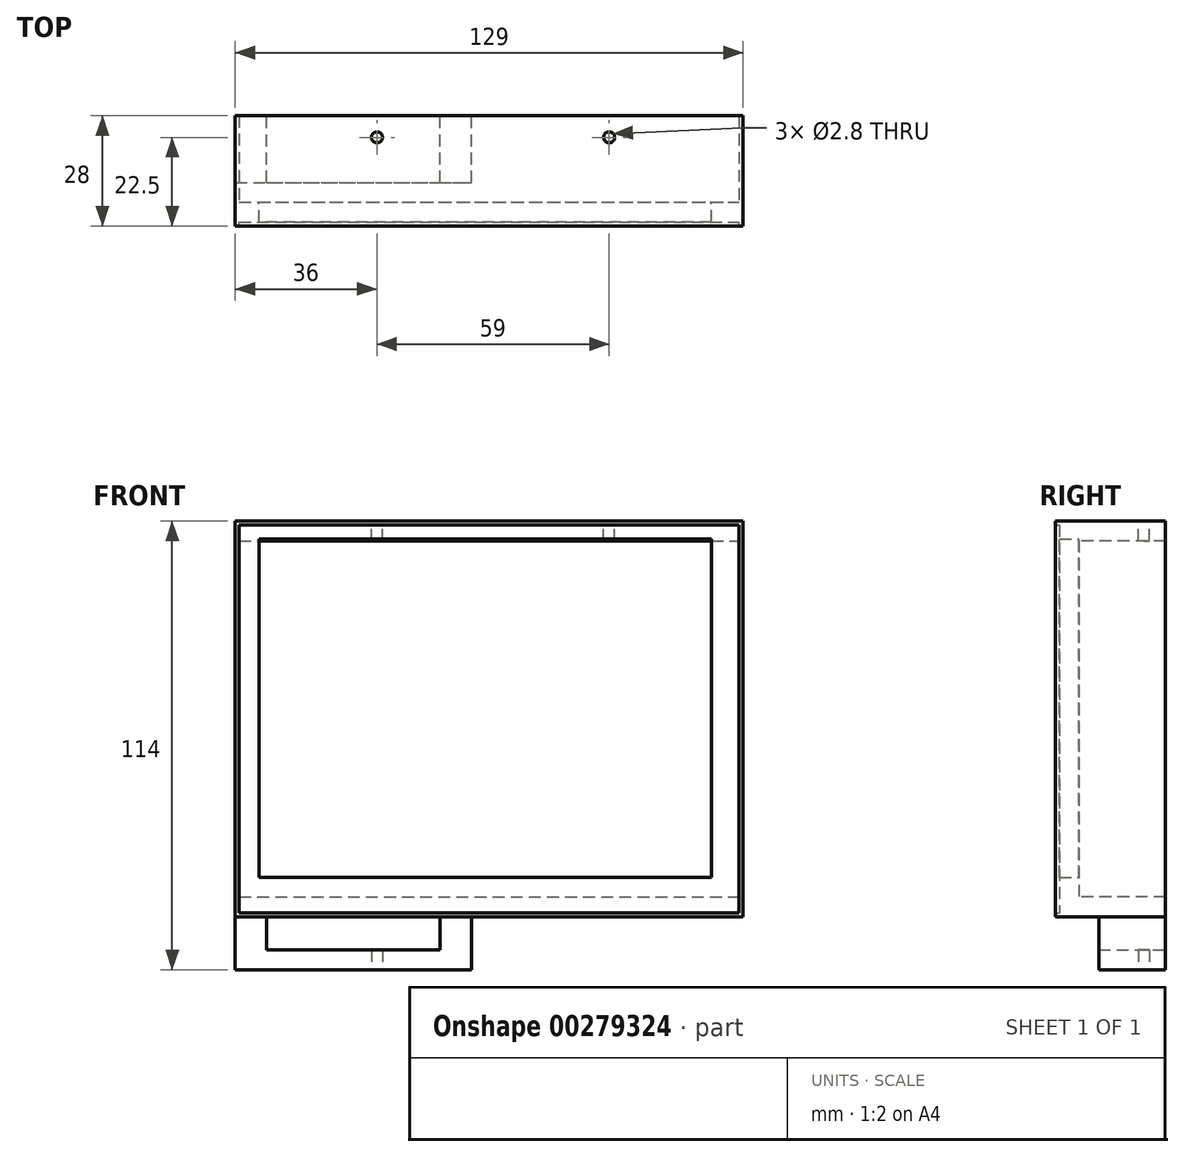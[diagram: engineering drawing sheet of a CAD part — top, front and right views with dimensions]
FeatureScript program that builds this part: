
annotation { "Feature Type Name" : "Feature", "Feature Type Description" : "" }
export const myFeature = defineFeature(function(context is Context, id is Id, definition is map)
    precondition{}
    {
        {
            var Q0;
            Q0=qCreatedBy(makeId("Front.planeOp"),FACE);
            var sketch = newSketch(context, id + "F0", { "sketchPlane" : qUnion([Q0])});
            skLineSegment(sketch, "E0.bottom", {"start": v(57.5, -43) * mm, "end": v(-57.5, -43) * mm});
            skLineSegment(sketch, "E0.top", {"start": v(57.5, 43) * mm, "end": v(-57.5, 43) * mm});
            skLineSegment(sketch, "E0.left", {"start": v(57.5, -43) * mm, "end": v(57.5, 43) * mm});
            skLineSegment(sketch, "E0.right", {"start": v(-57.5, -43) * mm, "end": v(-57.5, 43) * mm});
            skPoint(sketch, "E0.middle", {"position": v(0, 0) * mm});
            skLineSegment(sketch, "E1.bottom", {"start": v(-62.5, 46.5) * mm, "end": v(64.5, 46.5) * mm});
            skLineSegment(sketch, "E1.top", {"start": v(-62.5, -52) * mm, "end": v(64.5, -52) * mm});
            skLineSegment(sketch, "E1.left", {"start": v(-62.5, 46.5) * mm, "end": v(-62.5, -52) * mm});
            skLineSegment(sketch, "E1.right", {"start": v(64.5, 46.5) * mm, "end": v(64.5, -52) * mm});
            skSolve(sketch);
        }
        {
            var Q0;
            Q0=qCreatedBy(makeId("Front.planeOp"),FACE);
            var sketch = newSketch(context, id + "F1", { "sketchPlane" : qUnion([Q0])});
            skLineSegment(sketch, "E2.bottom", {"start": v(-62.5, 46.5) * mm, "end": v(64.5, 46.5) * mm});
            skLineSegment(sketch, "E2.top", {"start": v(-62.5, -52) * mm, "end": v(64.5, -52) * mm});
            skLineSegment(sketch, "E2.left", {"start": v(-62.5, 46.5) * mm, "end": v(-62.5, -52) * mm});
            skLineSegment(sketch, "E2.right", {"start": v(64.5, 46.5) * mm, "end": v(64.5, -52) * mm});
            skLineSegment(sketch, "E3.bottom", {"start": v(-63.5, 47.5) * mm, "end": v(65.5, 47.5) * mm});
            skLineSegment(sketch, "E3.top", {"start": v(-63.5, -53) * mm, "end": v(65.5, -53) * mm});
            skLineSegment(sketch, "E3.left", {"start": v(-63.5, 47.5) * mm, "end": v(-63.5, -53) * mm});
            skLineSegment(sketch, "E3.right", {"start": v(65.5, 47.5) * mm, "end": v(65.5, -53) * mm});
            skSolve(sketch);
        }
        {
            var Q0;
            Q0=qSketchRegion(id+"F1",true);
            extrude(context, id + "F2", {"entities" : qUnion([Q0]), "depth" : 6 * mm});
        }
        {
            var Q0;
            Q0=qCreatedBy(makeId("Front.planeOp"),FACE);
            var sketch = newSketch(context, id + "F3", { "sketchPlane" : qUnion([Q0])});
            skLineSegment(sketch, "E4.bottom", {"start": v(-63.5, 47.5) * mm, "end": v(65.5, 47.5) * mm});
            skLineSegment(sketch, "E4.top", {"start": v(-63.5, -53) * mm, "end": v(65.5, -53) * mm});
            skLineSegment(sketch, "E4.left", {"start": v(-63.5, 47.5) * mm, "end": v(-63.5, -53) * mm});
            skLineSegment(sketch, "E4.right", {"start": v(65.5, 47.5) * mm, "end": v(65.5, -53) * mm});
            skLineSegment(sketch, "E5.bottom", {"start": v(-62.5, 42.5) * mm, "end": v(64.5, 42.5) * mm});
            skLineSegment(sketch, "E5.top", {"start": v(-62.5, -48) * mm, "end": v(64.5, -48) * mm});
            skLineSegment(sketch, "E5.left", {"start": v(-62.5, 42.5) * mm, "end": v(-62.5, -48) * mm});
            skLineSegment(sketch, "E5.right", {"start": v(64.5, 42.5) * mm, "end": v(64.5, -48) * mm});
            skSolve(sketch);
        }
        {
            var Q0;
            Q0=qSketchRegion(id+"F3",true);
            extrude(context, id + "F4", {"entities" : qUnion([Q0]), "operationType" : NewBodyOperationType.ADD, "oppositeDirection" : true, "depth" : 22 * mm});
        }
        {
            var Q0;
            Q0=makeQuery(id+"F4.opExtrude","CAP_FACE",FACE,{"disambiguationData":[OSD([sQuery(id+"F3.wireOp",EDGE,"E4.bottom"),sQuery(id+"F3.wireOp",EDGE,"E4.top"),sQuery(id+"F3.wireOp",EDGE,"E4.left"),sQuery(id+"F3.wireOp",EDGE,"E4.right"),sQuery(id+"F3.wireOp",EDGE,"E5.bottom"),sQuery(id+"F3.wireOp",EDGE,"E5.top"),sQuery(id+"F3.wireOp",EDGE,"E5.left"),sQuery(id+"F3.wireOp",EDGE,"E5.right")])],"isStart":false});
            var sketch = newSketch(context, id + "F5", { "sketchPlane" : qUnion([Q0])});
            skLineSegment(sketch, "E6.top", {"start": v(63.5, -66.5) * mm, "end": v(3.5, -66.5) * mm});
            skLineSegment(sketch, "E6.left", {"start": v(63.5, -53) * mm, "end": v(63.5, -66.5) * mm});
            skLineSegment(sketch, "E6.right", {"start": v(3.5, -53) * mm, "end": v(3.5, -66.5) * mm});
            skLineSegment(sketch, "E7.top", {"start": v(55.5, -61.5) * mm, "end": v(11.5, -61.5) * mm});
            skLineSegment(sketch, "E7.left", {"start": v(55.5, -53) * mm, "end": v(55.5, -61.5) * mm});
            skLineSegment(sketch, "E7.right", {"start": v(11.5, -53) * mm, "end": v(11.5, -61.5) * mm});
            skLineSegment(sketch, "E8", {"start": v(63.5, -53) * mm, "end": v(55.5, -53) * mm});
            skLineSegment(sketch, "E9", {"start": v(11.5, -53) * mm, "end": v(3.5, -53) * mm});
            skSolve(sketch);
        }
        {
            var Q0;
            Q0 = qSketchRegion(id + "F5", true);
            extrude(context, id + "F6", {"entities" : qUnion([Q0]), "operationType" : NewBodyOperationType.ADD, "oppositeDirection" : true, "depth" : 17 * mm});
        }
        {
            var Q0;
            Q0=makeQuery(id+"F4.boolean.opBoolean","MERGE",FACE,{"derivedFrom":[makeQuery(id+"F2.opExtrude","SWEPT_FACE",FACE,{"disambiguationData":[OSD([sQuery(id+"F1.wireOp",EDGE,"E3.bottom")])]}),makeQuery(id+"F4.opExtrude","SWEPT_FACE",FACE,{"disambiguationData":[OSD([sQuery(id+"F3.wireOp",EDGE,"E4.bottom")])]})]});
            var sketch = newSketch(context, id + "F7", { "sketchPlane" : qUnion([Q0])});
            skCircle(sketch, "E10", {"center": v(-27.5, 16.5) * mm, "radius": 1.4 * mm});
            skCircle(sketch, "E11", {"center": v(31.5, 16.5) * mm, "radius": 1.4 * mm});
            skSolve(sketch);
        }
        {
            var Q0;
            Q0=qSketchRegion(id+"F7",true);
            extrude(context, id + "F8", {"entities" : qUnion([Q0]), "operationType" : NewBodyOperationType.REMOVE, "oppositeDirection" : true, "depth" : 7.9 * mm});
        }
        {
            var Q0;
            Q0=makeQuery(id+"F6.opExtrude","SWEPT_FACE",FACE,{"disambiguationData":[OSD([sQuery(id+"F5.wireOp",EDGE,"E6.top")])]});
            var sketch = newSketch(context, id + "F9", { "sketchPlane" : qUnion([Q0])});
            skCircle(sketch, "E12", {"center": v(-27.5, -16.5) * mm, "radius": 1.4 * mm});
            skSolve(sketch);
        }
        {
            var Q0;
            Q0 = qSketchRegion(id + "F9", true);
            extrude(context, id + "F10", {"entities" : qUnion([Q0]), "operationType" : NewBodyOperationType.REMOVE, "oppositeDirection" : true, "depth" : 5 * mm});
        }
        {
            var Q0;
            {var subQ0=sQuery(id+"F3.wireOp",EDGE,"E5.bottom");var subQ1=sQuery(id+"F3.wireOp",EDGE,"E5.left");var subQ2=sQuery(id+"F3.wireOp",EDGE,"E5.right");Q0=makeQuery(id+"F4.boolean.opBoolean","SPLIT",FACE,{"disambiguationData":[TD([makeQuery(id+"F2.opExtrude","SWEPT_FACE",FACE,{"disambiguationData":[OSD([sQuery(id+"F1.wireOp",EDGE,"E2.bottom")])]})])],"derivedFrom":makeQuery(id+"F4.opExtrude","CAP_FACE",FACE,{"disambiguationData":[OSD([sQuery(id+"F3.wireOp",EDGE,"E4.bottom"),sQuery(id+"F3.wireOp",EDGE,"E4.top"),sQuery(id+"F3.wireOp",EDGE,"E4.left"),sQuery(id+"F3.wireOp",EDGE,"E4.right"),subQ0,sQuery(id+"F3.wireOp",EDGE,"E5.top"),subQ1,subQ2])],"isStart":true})});}
            var sketch = newSketch(context, id + "F11", { "sketchPlane" : qUnion([Q0])});
            skLineSegment(sketch, "E13.bottom", {"start": v(57.5, -43) * mm, "end": v(-57.5, -43) * mm});
            skLineSegment(sketch, "E13.top", {"start": v(57.5, 43) * mm, "end": v(-57.5, 43) * mm});
            skLineSegment(sketch, "E13.left", {"start": v(57.5, -43) * mm, "end": v(57.5, 43) * mm});
            skLineSegment(sketch, "E13.right", {"start": v(-57.5, -43) * mm, "end": v(-57.5, 43) * mm});
            skPoint(sketch, "E13.middle", {"position": v(0, 0) * mm});
            skLineSegment(sketch, "E14.bottom", {"start": v(-62.5, 46.5) * mm, "end": v(64.5, 46.5) * mm});
            skLineSegment(sketch, "E14.top", {"start": v(-62.5, -52) * mm, "end": v(64.5, -52) * mm});
            skLineSegment(sketch, "E14.left", {"start": v(-62.5, 46.5) * mm, "end": v(-62.5, -52) * mm});
            skLineSegment(sketch, "E14.right", {"start": v(64.5, 46.5) * mm, "end": v(64.5, -52) * mm});
            skSolve(sketch);
        }
        {
            var Q0;
            Q0 = qSketchRegion(id + "F11", true);
            extrude(context, id + "F12", {"entities" : qUnion([Q0]), "operationType" : NewBodyOperationType.ADD, "depth" : 5 * mm});
        }
    });
